# Revit family: Magnuson-Taiga-CoatTrees++++++++++
name_source: partatom
category: Furniture
units: mm (PartAtom-declared; Revit-internal decimal feet)

## family parameters
Always vertical = Yes
Cut with Voids When Loaded = No
OmniClass Number = 23.40.20.00
OmniClass Title = General Furniture and Specialties
Room Calculation Point = No
Shared = No
Work Plane-Based = No

## types (1)
- TAIGA-01
    Assembly Code = E2020200
    Base Finish = MAG - Steel Painted
    Default Elevation = 0"
    Depth = 13 3/4"
    Description = Coat tree with painted steel base, aluminum painted post and 8 plastic coat hooks. Can be used with Mirac-6 plastic hangers. 69 3/4” x 13 3/4” x round
    Glides Finish = MAG - Plastic Black
    Height = 69 3/4"
    Hook Finish = MAG - Plastic Black
    Keynote = 12500
    Low Emitting Finish = Yes
    Low Emitting Material = Yes
    Manufacturer = Magnuson Group
    Model = TAIGA-01
    Percentage of Recycled Content = 0
    Post Finish = MAG - Aluminum Painted
    Product Documentation Link = https://magnusongroup.com
    Revit Model Built By = https://servex-us.com
    Salvage or Reuse = Yes
    Type Comments = Coat Tree
    URL = https://magnusongroup.com
    Width = 13 3/4"

## geometry (parser evidence)
native form markers: Sweep x4
no freeform markers — native parametric forms only
